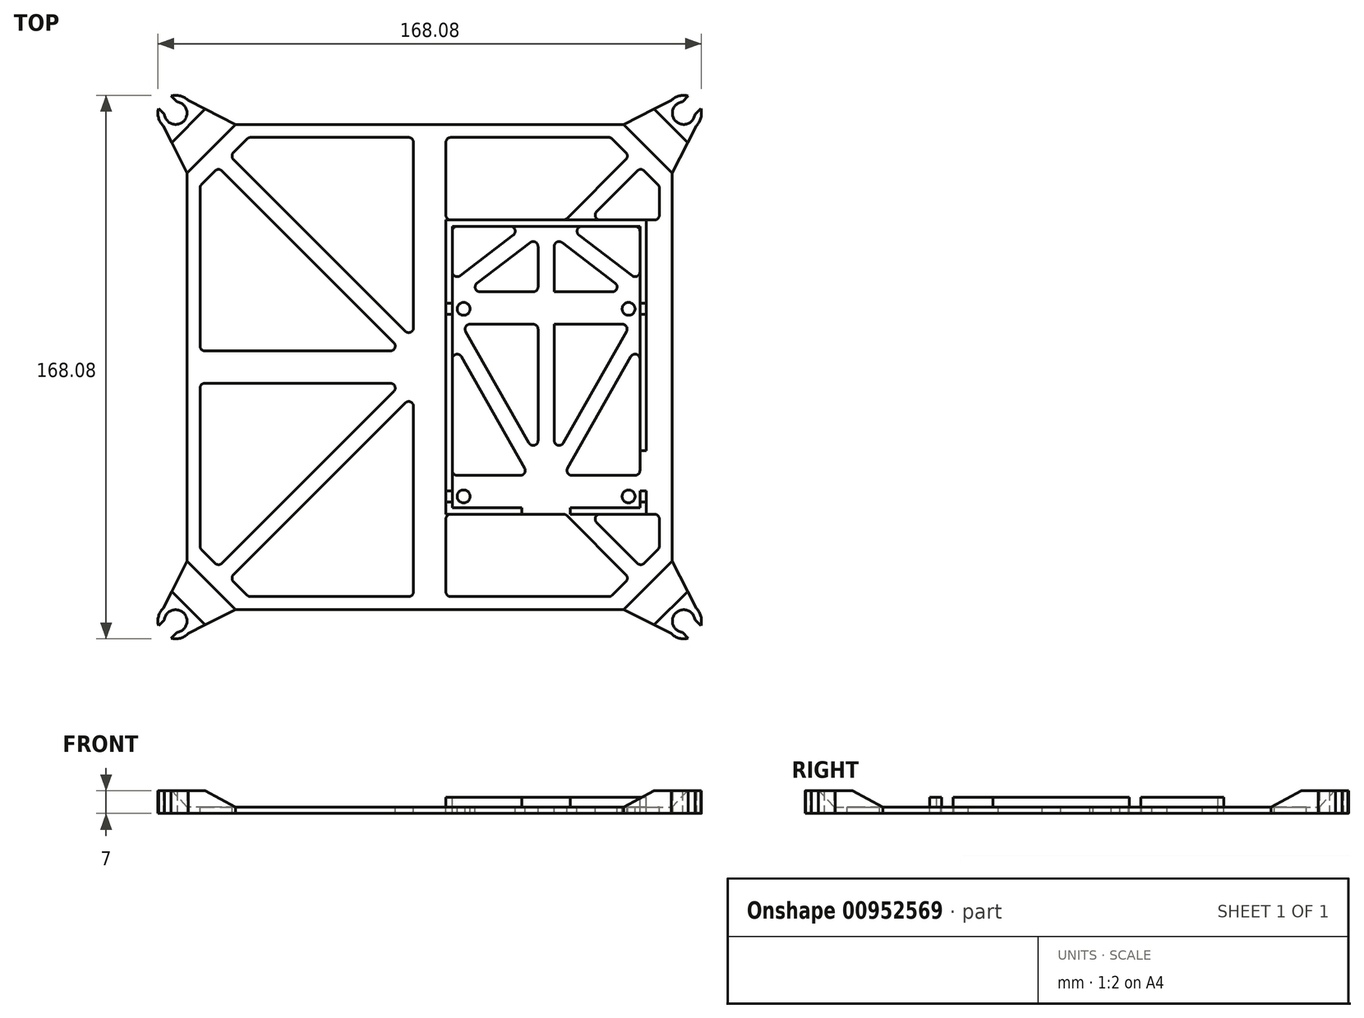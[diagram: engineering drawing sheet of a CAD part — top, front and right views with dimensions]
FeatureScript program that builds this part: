
annotation { "Feature Type Name" : "Feature", "Feature Type Description" : "" }
export const myFeature = defineFeature(function(context is Context, id is Id, definition is map)
    precondition{}
    {
        {
            var Q0;
            Q0=qCreatedBy(makeId("Top.planeOp"),FACE);
            var sketch = newSketch(context, id + "F0", { "sketchPlane" : qUnion([Q0])});
            skLineSegment(sketch, "E0.bottom", {"start": v(-75, 75) * mm, "end": v(75, 75) * mm});
            skLineSegment(sketch, "E0.top", {"start": v(-75, -75) * mm, "end": v(75, -75) * mm});
            skLineSegment(sketch, "E0.left", {"start": v(-75, 75) * mm, "end": v(-75, -75) * mm});
            skLineSegment(sketch, "E0.right", {"start": v(75, 75) * mm, "end": v(75, -75) * mm});
            skPoint(sketch, "E1", {"position": v(0, 75) * mm});
            skPoint(sketch, "E2", {"position": v(-75, 0) * mm});
            skSolve(sketch);
        }
        {
            var Q0;
            Q0=qSketchRegion(id+"F0",true);
            extrude(context, id + "F1", {"entities" : qUnion([Q0]), "depth" : 2 * mm, "offsetDistance" : 25 * mm});
        }
        {
            var Q0;
            Q0=makeQuery(id+"F1.opExtrude","CAP_FACE",FACE,{"disambiguationData":[OSD([sQuery(id+"F0.wireOp",EDGE,"E0.bottom"),sQuery(id+"F0.wireOp",EDGE,"E0.top"),sQuery(id+"F0.wireOp",EDGE,"E0.left"),sQuery(id+"F0.wireOp",EDGE,"E0.right")])],"isStart":false});
            var sketch = newSketch(context, id + "F2", { "sketchPlane" : qUnion([Q0])});
            skLineSegment(sketch, "E3.bottom", {"start": v(7, 43.5) * mm, "end": v(65, 43.5) * mm});
            skLineSegment(sketch, "E3.top", {"start": v(7, -43.5) * mm, "end": v(65, -43.5) * mm});
            skLineSegment(sketch, "E3.left", {"start": v(7, 43.5) * mm, "end": v(7, -43.5) * mm});
            skLineSegment(sketch, "E3.right", {"start": v(65, 43.5) * mm, "end": v(65, -43.5) * mm});
            skPoint(sketch, "E4", {"position": v(36, 43.5) * mm});
            skLineSegment(sketch, "E5.0", {"start": v(5, 45.5) * mm, "end": v(67, 45.5) * mm});
            skLineSegment(sketch, "E5.1", {"start": v(5, 45.5) * mm, "end": v(5, -45.5) * mm});
            skLineSegment(sketch, "E5.2", {"start": v(5, -45.5) * mm, "end": v(67, -45.5) * mm});
            skLineSegment(sketch, "E5.3", {"start": v(67, 45.5) * mm, "end": v(67, -45.5) * mm});
            skPoint(sketch, "E6", {"position": v(7, 0) * mm});
            skSolve(sketch);
        }
        {
            var Q0;
            Q0=qSketchRegion(id+"F2",true);
            extrude(context, id + "F3", {"entities" : qUnion([Q0]), "operationType" : NewBodyOperationType.ADD, "depth" : 3 * mm, "offsetDistance" : 25 * mm});
        }
        {
            var Q0;
            Q0=makeQuery(id+"F3.opExtrude","CAP_FACE",FACE,{"disambiguationData":[OSD([sQuery(id+"F2.wireOp",EDGE,"E3.bottom"),sQuery(id+"F2.wireOp",EDGE,"E3.top"),sQuery(id+"F2.wireOp",EDGE,"E3.left"),sQuery(id+"F2.wireOp",EDGE,"E3.right"),sQuery(id+"F2.wireOp",EDGE,"E5.0"),sQuery(id+"F2.wireOp",EDGE,"E5.1"),sQuery(id+"F2.wireOp",EDGE,"E5.2"),sQuery(id+"F2.wireOp",EDGE,"E5.3")])],"isStart":false});
            var sketch = newSketch(context, id + "F4", { "sketchPlane" : qUnion([Q0])});
            skLineSegment(sketch, "E7.bottom", {"start": v(28.5, -43.5) * mm, "end": v(43.5, -43.5) * mm});
            skLineSegment(sketch, "E7.top", {"start": v(28.5, -45.5) * mm, "end": v(43.5, -45.5) * mm});
            skLineSegment(sketch, "E7.left", {"start": v(28.5, -43.5) * mm, "end": v(28.5, -45.5) * mm});
            skLineSegment(sketch, "E7.right", {"start": v(43.5, -43.5) * mm, "end": v(43.5, -45.5) * mm});
            skLineSegment(sketch, "E8.bottom", {"start": v(67, -39.9) * mm, "end": v(65, -39.9) * mm});
            skLineSegment(sketch, "E8.top", {"start": v(67, -25.9) * mm, "end": v(65, -25.9) * mm});
            skLineSegment(sketch, "E8.left", {"start": v(67, -39.9) * mm, "end": v(67, -25.9) * mm});
            skLineSegment(sketch, "E8.right", {"start": v(65, -39.9) * mm, "end": v(65, -25.9) * mm});
            skPoint(sketch, "E9", {"position": v(36, -43.5) * mm});
            skPoint(sketch, "E10", {"position": v(36, -45.5) * mm});
            skPoint(sketch, "E11", {"position": v(65, -32.9) * mm});
            skSolve(sketch);
        }
        {
            var Q0;
            Q0=qSketchRegion(id+"F4",true);
            extrude(context, id + "F5", {"entities" : qUnion([Q0]), "operationType" : NewBodyOperationType.REMOVE, "oppositeDirection" : true, "depth" : 3 * mm, "offsetDistance" : 25 * mm});
        }
        {
            var Q0;
            {var subQ3=sQuery(id+"F4.wireOp",EDGE,"E7.bottom");Q0=makeQuery(id+"F4.imprint","IMPRINT",FACE,{"disambiguationData":[TD([[makeQuery(id+"F4.imprint","IMPRINT",EDGE,{"derivedFrom":subQ3}),1.0]])]});}
            var sketch = newSketch(context, id + "F6", { "sketchPlane" : qUnion([Q0])});
            skCircle(sketch, "E12", {"center": v(61.5, -40) * mm, "radius": 2 * mm});
            skCircle(sketch, "E13", {"center": v(61.5, 18) * mm, "radius": 2 * mm});
            skLineSegment(sketch, "E14", {"start": v(36, -43.5) * mm, "end": v(36, -14.74) * mm, "construction": true});
            skLineSegment(sketch, "E15.bottom", {"start": v(67, -41.75) * mm, "end": v(65, -41.75) * mm});
            skLineSegment(sketch, "E15.top", {"start": v(67, -38.25) * mm, "end": v(65, -38.25) * mm});
            skLineSegment(sketch, "E15.left", {"start": v(67, -41.75) * mm, "end": v(67, -38.25) * mm});
            skLineSegment(sketch, "E15.right", {"start": v(65, -41.75) * mm, "end": v(65, -38.25) * mm});
            skLineSegment(sketch, "E16.bottom", {"start": v(67, 19.75) * mm, "end": v(65, 19.75) * mm});
            skLineSegment(sketch, "E16.top", {"start": v(67, 16.25) * mm, "end": v(65, 16.25) * mm});
            skLineSegment(sketch, "E16.left", {"start": v(67, 19.75) * mm, "end": v(67, 16.25) * mm});
            skLineSegment(sketch, "E16.right", {"start": v(65, 19.75) * mm, "end": v(65, 16.25) * mm});
            skPoint(sketch, "E17", {"position": v(65, 18) * mm});
            skPoint(sketch, "E18", {"position": v(65, -40) * mm});
            skLineSegment(sketch, "E19.MirrorCS", {"start": v(5, -41.75) * mm, "end": v(7, -41.75) * mm});
            skLineSegment(sketch, "E20.MirrorCS", {"start": v(5, -41.75) * mm, "end": v(5, -38.25) * mm});
            skLineSegment(sketch, "E21.MirrorCS", {"start": v(7, -41.75) * mm, "end": v(7, -38.25) * mm});
            skLineSegment(sketch, "E22.MirrorCS", {"start": v(5, 16.25) * mm, "end": v(7, 16.25) * mm});
            skLineSegment(sketch, "E23.MirrorCS", {"start": v(5, -38.25) * mm, "end": v(7, -38.25) * mm});
            skLineSegment(sketch, "E24.MirrorCS", {"start": v(5, 19.75) * mm, "end": v(5, 16.25) * mm});
            skLineSegment(sketch, "E25.MirrorCS", {"start": v(7, 19.75) * mm, "end": v(7, 16.25) * mm});
            skLineSegment(sketch, "E26.MirrorCS", {"start": v(5, 19.75) * mm, "end": v(7, 19.75) * mm});
            skCircle(sketch, "E27.MirrorC", {"center": v(10.5, 18) * mm, "radius": 2 * mm});
            skCircle(sketch, "E28.MirrorC", {"center": v(10.5, -40) * mm, "radius": 2 * mm});
            skPoint(sketch, "E29.MirrorP", {"position": v(7, 18) * mm});
            skPoint(sketch, "E30.MirrorP", {"position": v(7, -40) * mm});
            skSolve(sketch);
        }
        {
            var Q0;
            Q0 = qSketchRegion(id + "F6", true);
            extrude(context, id + "F7", {"entities" : qUnion([Q0]), "operationType" : NewBodyOperationType.REMOVE, "oppositeDirection" : true, "depth" : 25 * mm, "offsetDistance" : 25 * mm});
        }
        {
            var Q0;
            Q0=makeQuery(id+"F2.imprint","IMPRINT",FACE,{"disambiguationData":[TD([[makeQuery(id+"F2.imprint","IMPRINT",EDGE,{"derivedFrom":sQuery(id+"F2.wireOp",EDGE,"E5.0")}),1.0]])]});
            var sketch = newSketch(context, id + "F8", { "sketchPlane" : qUnion([Q0])});
            skLineSegment(sketch, "E31", {"start": v(75, 75) * mm, "end": v(78.54, 78.54) * mm, "construction": true});
            skLineSegment(sketch, "E32", {"start": v(78.12, 82.01) * mm, "end": v(79.96, 83.85) * mm});
            skLineSegment(sketch, "E33", {"start": v(79.96, 83.85) * mm, "end": v(83.85, 79.96) * mm, "construction": true});
            skLineSegment(sketch, "E34", {"start": v(83.85, 79.96) * mm, "end": v(82.01, 78.12) * mm});
            skLineSegment(sketch, "E35", {"start": v(82.01, 78.12) * mm, "end": v(78.12, 82.01) * mm, "construction": true});
            skPoint(sketch, "E36", {"position": v(80.07, 80.07) * mm});
            skLineSegment(sketch, "E37.MirrorCS", {"start": v(83.85, 79.96) * mm, "end": v(85.69, 81.8) * mm, "construction": true});
            skLineSegment(sketch, "E38.MirrorCS", {"start": v(81.8, 85.69) * mm, "end": v(79.96, 83.85) * mm, "construction": true});
            skLineSegment(sketch, "E39.MirrorCS", {"start": v(85.69, 81.8) * mm, "end": v(81.8, 85.69) * mm, "construction": true});
            skArc(sketch, "E40", {"start": v(79.96, 83.85) * mm, "mid": v(77.11, 83.85) * mm, "end": v(74.65, 82.42) * mm});
            skArc(sketch, "E41", {"start": v(83.85, 79.96) * mm, "mid": v(82.42, 82.42) * mm, "end": v(79.96, 83.85) * mm, "construction": true});
            skArc(sketch, "E42", {"start": v(82.01, 78.12) * mm, "mid": v(81.01, 81.01) * mm, "end": v(78.12, 82.01) * mm, "construction": true});
            skArc(sketch, "E43", {"start": v(78.12, 82.01) * mm, "mid": v(76.06, 76.06) * mm, "end": v(82.01, 78.12) * mm});
            skLineSegment(sketch, "E44", {"start": v(74.65, 82.42) * mm, "end": v(82.42, 74.65) * mm, "construction": true});
            skLineSegment(sketch, "E45", {"start": v(74.65, 82.42) * mm, "end": v(60, 75) * mm});
            skLineSegment(sketch, "E46.MirrorCS", {"start": v(82.42, 74.65) * mm, "end": v(75, 60) * mm});
            skArc(sketch, "E47", {"start": v(82.42, 74.65) * mm, "mid": v(83.85, 77.11) * mm, "end": v(83.85, 79.96) * mm});
            skArc(sketch, "E48", {"start": v(74.65, 82.42) * mm, "mid": v(74.65, 74.65) * mm, "end": v(82.42, 74.65) * mm, "construction": true});
            skLineSegment(sketch, "E49.2.8", {"start": v(-75, -75) * mm, "end": v(75, 75) * mm, "construction": true});
            skLineSegment(sketch, "E50", {"start": v(60, 75) * mm, "end": v(75, 60) * mm});
            skLineSegment(sketch, "E51.1.0", {"start": v(-74.65, 82.42) * mm, "end": v(-60, 75) * mm});
            skArc(sketch, "E51.1.1", {"start": v(-82.42, 74.65) * mm, "mid": v(-74.65, 74.65) * mm, "end": v(-74.65, 82.42) * mm, "construction": true});
            skLineSegment(sketch, "E51.1.2", {"start": v(-82.42, 74.65) * mm, "end": v(-75, 60) * mm});
            skLineSegment(sketch, "E51.1.3", {"start": v(-75, 60) * mm, "end": v(-60, 75) * mm});
            skPoint(sketch, "E51.1.4", {"position": v(-78.54, 78.54) * mm});
            skArc(sketch, "E51.1.5", {"start": v(-82.01, 78.12) * mm, "mid": v(-76.06, 76.06) * mm, "end": v(-78.12, 82.01) * mm});
            skLineSegment(sketch, "E51.1.6", {"start": v(-81.8, 85.69) * mm, "end": v(-85.69, 81.8) * mm, "construction": true});
            skPoint(sketch, "E51.1.7", {"position": v(-80.07, 80.07) * mm});
            skLineSegment(sketch, "E51.1.8", {"start": v(-75, 75) * mm, "end": v(-78.54, 78.54) * mm, "construction": true});
            skLineSegment(sketch, "E51.1.9", {"start": v(-82.42, 74.65) * mm, "end": v(-74.65, 82.42) * mm, "construction": true});
            skArc(sketch, "E51.1.10", {"start": v(-78.12, 82.01) * mm, "mid": v(-81.01, 81.01) * mm, "end": v(-82.01, 78.12) * mm, "construction": true});
            skArc(sketch, "E51.1.11", {"start": v(-74.65, 82.42) * mm, "mid": v(-77.11, 83.85) * mm, "end": v(-79.96, 83.85) * mm});
            skArc(sketch, "E51.1.12", {"start": v(-83.85, 79.96) * mm, "mid": v(-83.85, 77.11) * mm, "end": v(-82.42, 74.65) * mm});
            skLineSegment(sketch, "E51.1.13", {"start": v(-78.12, 82.01) * mm, "end": v(-82.01, 78.12) * mm, "construction": true});
            skLineSegment(sketch, "E51.1.14", {"start": v(-83.85, 79.96) * mm, "end": v(-79.96, 83.85) * mm, "construction": true});
            skLineSegment(sketch, "E51.1.15", {"start": v(-85.69, 81.8) * mm, "end": v(-83.85, 79.96) * mm, "construction": true});
            skLineSegment(sketch, "E51.1.16", {"start": v(-79.96, 83.85) * mm, "end": v(-78.12, 82.01) * mm});
            skLineSegment(sketch, "E51.1.17", {"start": v(-79.96, 83.85) * mm, "end": v(-81.8, 85.69) * mm, "construction": true});
            skArc(sketch, "E51.1.18", {"start": v(-79.96, 83.85) * mm, "mid": v(-82.42, 82.42) * mm, "end": v(-83.85, 79.96) * mm, "construction": true});
            skLineSegment(sketch, "E51.1.19", {"start": v(-82.01, 78.12) * mm, "end": v(-83.85, 79.96) * mm});
            skLineSegment(sketch, "E51.2.0", {"start": v(-82.42, -74.65) * mm, "end": v(-75, -60) * mm});
            skArc(sketch, "E51.2.1", {"start": v(-74.65, -82.42) * mm, "mid": v(-74.65, -74.65) * mm, "end": v(-82.42, -74.65) * mm, "construction": true});
            skLineSegment(sketch, "E51.2.2", {"start": v(-74.65, -82.42) * mm, "end": v(-60, -75) * mm});
            skLineSegment(sketch, "E51.2.3", {"start": v(-60, -75) * mm, "end": v(-75, -60) * mm});
            skPoint(sketch, "E51.2.4", {"position": v(-78.54, -78.54) * mm});
            skArc(sketch, "E51.2.5", {"start": v(-78.12, -82.01) * mm, "mid": v(-76.06, -76.06) * mm, "end": v(-82.01, -78.12) * mm});
            skLineSegment(sketch, "E51.2.6", {"start": v(-85.69, -81.8) * mm, "end": v(-81.8, -85.69) * mm, "construction": true});
            skPoint(sketch, "E51.2.7", {"position": v(-80.07, -80.07) * mm});
            skLineSegment(sketch, "E51.2.8", {"start": v(-75, -75) * mm, "end": v(-78.54, -78.54) * mm, "construction": true});
            skLineSegment(sketch, "E51.2.9", {"start": v(-74.65, -82.42) * mm, "end": v(-82.42, -74.65) * mm, "construction": true});
            skArc(sketch, "E51.2.10", {"start": v(-82.01, -78.12) * mm, "mid": v(-81.01, -81.01) * mm, "end": v(-78.12, -82.01) * mm, "construction": true});
            skArc(sketch, "E51.2.11", {"start": v(-82.42, -74.65) * mm, "mid": v(-83.85, -77.11) * mm, "end": v(-83.85, -79.96) * mm});
            skArc(sketch, "E51.2.12", {"start": v(-79.96, -83.85) * mm, "mid": v(-77.11, -83.85) * mm, "end": v(-74.65, -82.42) * mm});
            skLineSegment(sketch, "E51.2.13", {"start": v(-82.01, -78.12) * mm, "end": v(-78.12, -82.01) * mm, "construction": true});
            skLineSegment(sketch, "E51.2.14", {"start": v(-79.96, -83.85) * mm, "end": v(-83.85, -79.96) * mm, "construction": true});
            skLineSegment(sketch, "E51.2.15", {"start": v(-81.8, -85.69) * mm, "end": v(-79.96, -83.85) * mm, "construction": true});
            skLineSegment(sketch, "E51.2.16", {"start": v(-83.85, -79.96) * mm, "end": v(-82.01, -78.12) * mm});
            skLineSegment(sketch, "E51.2.17", {"start": v(-83.85, -79.96) * mm, "end": v(-85.69, -81.8) * mm, "construction": true});
            skArc(sketch, "E51.2.18", {"start": v(-83.85, -79.96) * mm, "mid": v(-82.42, -82.42) * mm, "end": v(-79.96, -83.85) * mm, "construction": true});
            skLineSegment(sketch, "E51.2.19", {"start": v(-78.12, -82.01) * mm, "end": v(-79.96, -83.85) * mm});
            skPoint(sketch, "E51.center", {"position": v(0, 0) * mm});
            skLineSegment(sketch, "E52.2.3.0", {"start": v(74.65, -82.42) * mm, "end": v(60, -75) * mm});
            skArc(sketch, "E52.3.3.0", {"start": v(82.42, -74.65) * mm, "mid": v(74.65, -74.65) * mm, "end": v(74.65, -82.42) * mm, "construction": true});
            skLineSegment(sketch, "E52.7.3.0", {"start": v(82.42, -74.65) * mm, "end": v(75, -60) * mm});
            skLineSegment(sketch, "E52.10.3.0", {"start": v(75, -60) * mm, "end": v(60, -75) * mm});
            skPoint(sketch, "E52.13.3.0", {"position": v(78.54, -78.54) * mm});
            skArc(sketch, "E52.14.3.0", {"start": v(82.01, -78.12) * mm, "mid": v(76.06, -76.06) * mm, "end": v(78.12, -82.01) * mm});
            skLineSegment(sketch, "E52.18.3.0", {"start": v(81.8, -85.69) * mm, "end": v(85.69, -81.8) * mm, "construction": true});
            skPoint(sketch, "E52.21.3.0", {"position": v(80.07, -80.07) * mm});
            skLineSegment(sketch, "E52.22.3.0", {"start": v(75, -75) * mm, "end": v(78.54, -78.54) * mm, "construction": true});
            skLineSegment(sketch, "E52.25.3.0", {"start": v(82.42, -74.65) * mm, "end": v(74.65, -82.42) * mm, "construction": true});
            skArc(sketch, "E52.28.3.0", {"start": v(78.12, -82.01) * mm, "mid": v(81.01, -81.01) * mm, "end": v(82.01, -78.12) * mm, "construction": true});
            skArc(sketch, "E52.32.3.0", {"start": v(74.65, -82.42) * mm, "mid": v(77.11, -83.85) * mm, "end": v(79.96, -83.85) * mm});
            skArc(sketch, "E52.36.3.0", {"start": v(83.85, -79.96) * mm, "mid": v(83.85, -77.11) * mm, "end": v(82.42, -74.65) * mm});
            skLineSegment(sketch, "E52.40.3.0", {"start": v(78.12, -82.01) * mm, "end": v(82.01, -78.12) * mm, "construction": true});
            skLineSegment(sketch, "E52.43.3.0", {"start": v(83.85, -79.96) * mm, "end": v(79.96, -83.85) * mm, "construction": true});
            skLineSegment(sketch, "E52.46.3.0", {"start": v(85.69, -81.8) * mm, "end": v(83.85, -79.96) * mm, "construction": true});
            skLineSegment(sketch, "E52.49.3.0", {"start": v(79.96, -83.85) * mm, "end": v(78.12, -82.01) * mm});
            skLineSegment(sketch, "E52.52.3.0", {"start": v(79.96, -83.85) * mm, "end": v(81.8, -85.69) * mm, "construction": true});
            skArc(sketch, "E52.55.3.0", {"start": v(79.96, -83.85) * mm, "mid": v(82.42, -82.42) * mm, "end": v(83.85, -79.96) * mm, "construction": true});
            skLineSegment(sketch, "E52.59.3.0", {"start": v(82.01, -78.12) * mm, "end": v(83.85, -79.96) * mm});
            skSolve(sketch);
        }
        {
            var Q0;
            Q0 = qSketchRegion(id + "F8", true);
            extrude(context, id + "F9", {"entities" : qUnion([Q0]), "operationType" : NewBodyOperationType.ADD, "depth" : 5 * mm, "offsetDistance" : 25 * mm, "hasSecondDirection" : true, "secondDirectionOppositeDirection" : true, "secondDirectionDepth" : 2 * mm});
        }
        {
            var Q0;
            Q0 = qSketchRegion(id + "F8", true);
            extrude(context, id + "F10", {"entities" : qUnion([Q0]), "operationType" : NewBodyOperationType.ADD, "depth" : 5 * mm, "offsetDistance" : 25 * mm});
        }
        {
            var Q0;
            Q0 = qSketchRegion(id + "F8", true);
            extrude(context, id + "F11", {"entities" : qUnion([Q0]), "operationType" : NewBodyOperationType.ADD, "depth" : 5 * mm, "offsetDistance" : 25 * mm});
        }
        {
            var Q0;
            Q0=makeQuery(id+"F9.opExtrude","CAP_EDGE",EDGE,{"disambiguationData":[OSD([sQuery(id+"F8.wireOp",EDGE,"E51.1.3")])],"isStart":false});
            var Q1;
            Q1=makeQuery(id+"F9.opExtrude","CAP_EDGE",EDGE,{"disambiguationData":[OSD([sQuery(id+"F8.wireOp",EDGE,"E50")])],"isStart":false});
            var Q2;
            Q2=makeQuery(id+"F9.opExtrude","CAP_EDGE",EDGE,{"disambiguationData":[OSD([sQuery(id+"F8.wireOp",EDGE,"E52.10.3.0")])],"isStart":false});
            var Q3;
            Q3=makeQuery(id+"F9.opExtrude","CAP_EDGE",EDGE,{"disambiguationData":[OSD([sQuery(id+"F8.wireOp",EDGE,"E51.2.3")])],"isStart":false});
            chamfer(context, id + "F12", {"entities" : qUnion([Q0, Q1, Q2, Q3]), "chamferType" : ChamferType.TWO_OFFSETS, "width1" : 10 * mm, "oppositeDirection" : false, "width2" : 5 * mm, "tangentPropagation" : true});
        }
        {
            var Q0;
            Q0=makeQuery(id+"F2.imprint","IMPRINT",FACE,{"disambiguationData":[TD([[makeQuery(id+"F2.imprint","IMPRINT",EDGE,{"derivedFrom":sQuery(id+"F2.wireOp",EDGE,"E5.0")}),1.0]])]});
            var sketch = newSketch(context, id + "F13", { "sketchPlane" : qUnion([Q0])});
            skLineSegment(sketch, "E53", {"start": v(-71, -56) * mm, "end": v(-71, 56) * mm, "construction": true});
            skLineSegment(sketch, "E54", {"start": v(-60.67, 66.33) * mm, "end": v(-56, 71) * mm, "construction": true});
            skLineSegment(sketch, "E55", {"start": v(-75, 60) * mm, "end": v(60, -75) * mm, "construction": true});
            skLineSegment(sketch, "E56", {"start": v(-75, -60) * mm, "end": v(60, 75) * mm, "construction": true});
            skLineSegment(sketch, "E57.1.0", {"start": v(-56, -71) * mm, "end": v(-71, -56) * mm, "construction": true});
            skLineSegment(sketch, "E57.1.1", {"start": v(56, -71) * mm, "end": v(-56, -71) * mm, "construction": true});
            skLineSegment(sketch, "E57.2.0", {"start": v(71, -56) * mm, "end": v(56, -71) * mm, "construction": true});
            skLineSegment(sketch, "E57.2.1", {"start": v(71, 56) * mm, "end": v(71, -56) * mm, "construction": true});
            skLineSegment(sketch, "E57.3.0", {"start": v(56, 71) * mm, "end": v(71, 56) * mm, "construction": true});
            skLineSegment(sketch, "E57.3.1", {"start": v(-56, 71) * mm, "end": v(-6.5, 71) * mm, "construction": true});
            skPoint(sketch, "E57.center", {"position": v(0, 0) * mm});
            skLineSegment(sketch, "E58", {"start": v(-71, 56) * mm, "end": v(-71, -56) * mm});
            skLineSegment(sketch, "E59", {"start": v(-5, 69.5) * mm, "end": v(-5, 12.16) * mm, "construction": true});
            skLineSegment(sketch, "E60", {"start": v(5, 71) * mm, "end": v(5, 45.5) * mm});
            skLineSegment(sketch, "E61", {"start": v(5, -45.5) * mm, "end": v(5, -71) * mm});
            skLineSegment(sketch, "E62", {"start": v(-71, 5) * mm, "end": v(-8.54, 5) * mm});
            skLineSegment(sketch, "E63", {"start": v(-71, -5) * mm, "end": v(0, -5) * mm});
            skLineSegment(sketch, "E64", {"start": v(-60.67, 64.2) * mm, "end": v(-7.56, 11.1) * mm});
            skLineSegment(sketch, "E65", {"start": v(-65.27, 61.73) * mm, "end": v(-8.54, 5) * mm});
            skPoint(sketch, "E66", {"position": v(-63.5, 63.5) * mm});
            skLineSegment(sketch, "E67", {"start": v(-63.5, 63.5) * mm, "end": v(75.2, -75.2) * mm, "construction": true});
            skLineSegment(sketch, "E68", {"start": v(-5, 71) * mm, "end": v(-56, 71) * mm});
            skLineSegment(sketch, "E69", {"start": v(-61.73, 65.27) * mm, "end": v(-56, 71) * mm});
            skLineSegment(sketch, "E70", {"start": v(-65.27, 61.73) * mm, "end": v(-71, 56) * mm});
            skLineSegment(sketch, "E71", {"start": v(-71, 5) * mm, "end": v(-71, 56) * mm});
            skLineSegment(sketch, "E72", {"start": v(0, 0) * mm, "end": v(-75, 0) * mm, "construction": true});
            skLineSegment(sketch, "E73.MirrorCS", {"start": v(-71, -5) * mm, "end": v(-71, -56) * mm});
            skLineSegment(sketch, "E74.MirrorCS", {"start": v(-65.27, -61.73) * mm, "end": v(-71, -56) * mm});
            skLineSegment(sketch, "E75.MirrorCS", {"start": v(-61.73, -65.27) * mm, "end": v(-56, -71) * mm});
            skLineSegment(sketch, "E76.MirrorCS", {"start": v(-5, -71) * mm, "end": v(-56, -71) * mm});
            skLineSegment(sketch, "E77.MirrorCS", {"start": v(-71, -56) * mm, "end": v(-71, 56) * mm});
            skLineSegment(sketch, "E78.MirrorCS", {"start": v(-61.73, -65.27) * mm, "end": v(-5, -8.54) * mm});
            skLineSegment(sketch, "E79.MirrorCS", {"start": v(-65.27, -61.73) * mm, "end": v(-8.54, -5) * mm});
            skPoint(sketch, "E80.MirrorP", {"position": v(-63.5, -63.5) * mm});
            skLineSegment(sketch, "E81.MirrorCS", {"start": v(-56, -71) * mm, "end": v(56, -71) * mm, "construction": true});
            skLineSegment(sketch, "E82.MirrorCS", {"start": v(-71, -56) * mm, "end": v(-56, -71) * mm, "construction": true});
            skLineSegment(sketch, "E83.MirrorCS", {"start": v(-63.5, -63.5) * mm, "end": v(75.2, 75.2) * mm, "construction": true});
            skLineSegment(sketch, "E84.MirrorCS", {"start": v(-5, -71) * mm, "end": v(-5, 8.54) * mm});
            skLineSegment(sketch, "E85", {"start": v(-5, 8.54) * mm, "end": v(-5, 71) * mm});
            skLineSegment(sketch, "E86", {"start": v(-8.54, 5) * mm, "end": v(0, 5) * mm, "construction": true});
            skLineSegment(sketch, "E87", {"start": v(-5, 8.54) * mm, "end": v(-5, 71) * mm, "construction": true});
            skLineSegment(sketch, "E88", {"start": v(-5, -8.54) * mm, "end": v(-5, -71) * mm, "construction": true});
            skLineSegment(sketch, "E89", {"start": v(5, -71) * mm, "end": v(56, -71) * mm});
            skLineSegment(sketch, "E90", {"start": v(5, 71) * mm, "end": v(56, 71) * mm});
            skLineSegment(sketch, "E91", {"start": v(56, 71) * mm, "end": v(61.73, 65.27) * mm});
            skLineSegment(sketch, "E92", {"start": v(61.73, 65.27) * mm, "end": v(41.96, 45.5) * mm});
            skLineSegment(sketch, "E93", {"start": v(41.96, 45.5) * mm, "end": v(5, 45.5) * mm});
            skLineSegment(sketch, "E94", {"start": v(5, -45.5) * mm, "end": v(41.96, -45.5) * mm});
            skLineSegment(sketch, "E95", {"start": v(41.96, -45.5) * mm, "end": v(61.73, -65.27) * mm});
            skLineSegment(sketch, "E96", {"start": v(61.73, -65.27) * mm, "end": v(56, -71) * mm});
            skLineSegment(sketch, "E97", {"start": v(65.27, 61.73) * mm, "end": v(49.04, 45.5) * mm});
            skLineSegment(sketch, "E98", {"start": v(49.04, 45.5) * mm, "end": v(71, 45.5) * mm});
            skLineSegment(sketch, "E99", {"start": v(71, 45.5) * mm, "end": v(71, 56) * mm});
            skLineSegment(sketch, "E100", {"start": v(65.27, 61.73) * mm, "end": v(71, 56) * mm});
            skLineSegment(sketch, "E101", {"start": v(49.04, -45.5) * mm, "end": v(65.27, -61.73) * mm});
            skLineSegment(sketch, "E102", {"start": v(65.27, -61.73) * mm, "end": v(71, -56) * mm});
            skLineSegment(sketch, "E103", {"start": v(71, -45.5) * mm, "end": v(49.04, -45.5) * mm});
            skLineSegment(sketch, "E104", {"start": v(71, -45.5) * mm, "end": v(71, -56) * mm});
            skPoint(sketch, "E105.newPointA", {"position": v(56, 71) * mm});
            skPoint(sketch, "E105.newPointB", {"position": v(-5, 71) * mm});
            skArc(sketch, "E105.filletArc", {"start": v(-5, 69.5) * mm, "mid": v(-5.44, 70.56) * mm, "end": v(-6.5, 71) * mm, "construction": true});
            skPoint(sketch, "E106.newPointA", {"position": v(-71, 56) * mm});
            skPoint(sketch, "E106.newPointB", {"position": v(-61.73, 65.27) * mm});
            skArc(sketch, "E106.filletArc", {"start": v(-60.67, 66.33) * mm, "mid": v(-61.11, 65.27) * mm, "end": v(-60.67, 64.2) * mm});
            skPoint(sketch, "E107.newPointA", {"position": v(-5, -71) * mm});
            skPoint(sketch, "E107.newPointB", {"position": v(-5, 8.54) * mm});
            skArc(sketch, "E107.filletArc", {"start": v(-7.56, 11.1) * mm, "mid": v(-5.93, 10.77) * mm, "end": v(-5, 12.16) * mm});
            skSolve(sketch);
        }
        {
            var Q0;
            Q0 = qSketchRegion(id + "F13", true);
            extrude(context, id + "F14", {"entities" : qUnion([Q0]), "operationType" : NewBodyOperationType.REMOVE, "oppositeDirection" : true, "depth" : 25 * mm, "offsetDistance" : 25 * mm});
        }
        {
            var Q0;
            {var subQ3=sQuery(id+"F4.wireOp",EDGE,"E7.bottom");Q0=makeQuery(id+"F4.imprint","IMPRINT",FACE,{"disambiguationData":[TD([[makeQuery(id+"F4.imprint","IMPRINT",EDGE,{"derivedFrom":subQ3}),1.0]])]});}
            var sketch = newSketch(context, id + "F15", { "sketchPlane" : qUnion([Q0])});
            skLineSegment(sketch, "E108", {"start": v(7, 23.25) * mm, "end": v(11.12, 23.25) * mm, "construction": true});
            skLineSegment(sketch, "E109", {"start": v(7, 13.25) * mm, "end": v(9.87, 13.25) * mm, "construction": true});
            skLineSegment(sketch, "E110", {"start": v(33.5, 43.5) * mm, "end": v(33.5, 40.35) * mm, "construction": true});
            skLineSegment(sketch, "E111", {"start": v(38.5, 43.5) * mm, "end": v(38.5, 23.25) * mm});
            skLineSegment(sketch, "E112", {"start": v(8.5, -33.5) * mm, "end": v(28.05, -33.5) * mm});
            skLineSegment(sketch, "E113", {"start": v(33.5, 11.75) * mm, "end": v(33.5, -22.74) * mm});
            skLineSegment(sketch, "E114", {"start": v(38.5, 13.25) * mm, "end": v(38.5, -33.5) * mm});
            skLineSegment(sketch, "E115", {"start": v(7, 23.25) * mm, "end": v(7, 13.25) * mm, "construction": true});
            skPoint(sketch, "E116", {"position": v(7, 18.25) * mm});
            skLineSegment(sketch, "E117", {"start": v(33.5, 43.5) * mm, "end": v(38.5, 43.5) * mm, "construction": true});
            skPoint(sketch, "E118", {"position": v(36, 43.5) * mm});
            skLineSegment(sketch, "E119", {"start": v(38.5, 23.25) * mm, "end": v(65, 23.25) * mm});
            skLineSegment(sketch, "E120", {"start": v(33.5, 23.25) * mm, "end": v(38.5, 23.25) * mm, "construction": true});
            skLineSegment(sketch, "E121", {"start": v(33.5, 13.25) * mm, "end": v(38.5, 13.25) * mm, "construction": true});
            skLineSegment(sketch, "E122", {"start": v(38.5, 13.25) * mm, "end": v(65, 13.25) * mm});
            skLineSegment(sketch, "E123", {"start": v(38.5, -33.5) * mm, "end": v(38.5, -33.5) * mm});
            skLineSegment(sketch, "E124", {"start": v(33.5, -33.5) * mm, "end": v(38.5, -33.5) * mm, "construction": true});
            skLineSegment(sketch, "E125", {"start": v(38.5, -33.5) * mm, "end": v(65, -33.5) * mm});
            skLineSegment(sketch, "E126", {"start": v(11.14, 11.01) * mm, "end": v(30.7, -23.48) * mm});
            skLineSegment(sketch, "E127", {"start": v(9.8, 3.23) * mm, "end": v(29.36, -31.26) * mm});
            skLineSegment(sketch, "E128", {"start": v(7, 13.25) * mm, "end": v(33.5, -33.5) * mm, "construction": true});
            skLineSegment(sketch, "E129", {"start": v(12.45, 13.25) * mm, "end": v(32, 13.25) * mm});
            skLineSegment(sketch, "E130", {"start": v(7, 2.5) * mm, "end": v(7, -32) * mm});
            skPoint(sketch, "E131.visualSharp", {"position": v(7, 8.18) * mm});
            skArc(sketch, "E131.filletArc", {"start": v(9.8, 3.23) * mm, "mid": v(8.12, 3.94) * mm, "end": v(7, 2.5) * mm});
            skArc(sketch, "E132.filletArc", {"start": v(28.05, -33.5) * mm, "mid": v(29.35, -32.76) * mm, "end": v(29.36, -31.26) * mm});
            skPoint(sketch, "E133.visualSharp", {"position": v(7, -33.5) * mm});
            skArc(sketch, "E133.filletArc", {"start": v(7, -32) * mm, "mid": v(7.44, -33.06) * mm, "end": v(8.5, -33.5) * mm});
            skPoint(sketch, "E134.visualSharp", {"position": v(9.87, 13.25) * mm});
            skArc(sketch, "E134.filletArc", {"start": v(12.45, 13.25) * mm, "mid": v(11.15, 12.5) * mm, "end": v(11.14, 11.01) * mm});
            skPoint(sketch, "E135.visualSharp", {"position": v(33.5, 13.25) * mm});
            skArc(sketch, "E135.filletArc", {"start": v(33.5, 11.75) * mm, "mid": v(33.06, 12.81) * mm, "end": v(32, 13.25) * mm});
            skArc(sketch, "E136.filletArc", {"start": v(30.7, -23.48) * mm, "mid": v(32.38, -24.2) * mm, "end": v(33.5, -22.74) * mm});
            skLineSegment(sketch, "E137", {"start": v(36, -43.5) * mm, "end": v(36, -5.37) * mm, "construction": true});
            skArc(sketch, "E138.MirrorCS", {"start": v(65, -32) * mm, "mid": v(64.56, -33.06) * mm, "end": v(63.5, -33.5) * mm});
            skArc(sketch, "E139.MirrorCS", {"start": v(62.2, 3.23) * mm, "mid": v(63.88, 3.94) * mm, "end": v(65, 2.5) * mm});
            skArc(sketch, "E140.MirrorCS", {"start": v(43.95, -33.5) * mm, "mid": v(42.65, -32.76) * mm, "end": v(42.64, -31.26) * mm});
            skArc(sketch, "E141.MirrorCS", {"start": v(38.5, 11.75) * mm, "mid": v(38.94, 12.81) * mm, "end": v(40, 13.25) * mm});
            skLineSegment(sketch, "E142.MirrorCS", {"start": v(38.5, 13.25) * mm, "end": v(33.5, 13.25) * mm, "construction": true});
            skLineSegment(sketch, "E143.MirrorCS", {"start": v(65, 13.25) * mm, "end": v(62.13, 13.25) * mm, "construction": true});
            skArc(sketch, "E144.MirrorCS", {"start": v(59.55, 13.25) * mm, "mid": v(60.85, 12.5) * mm, "end": v(60.86, 11.01) * mm});
            skLineSegment(sketch, "E145.MirrorCS", {"start": v(38.5, -33.5) * mm, "end": v(33.5, -33.5) * mm, "construction": true});
            skArc(sketch, "E146.MirrorCS", {"start": v(41.3, -23.48) * mm, "mid": v(39.62, -24.2) * mm, "end": v(38.5, -22.74) * mm});
            skLineSegment(sketch, "E147.MirrorCS", {"start": v(65, 13.25) * mm, "end": v(38.5, -33.5) * mm, "construction": true});
            skLineSegment(sketch, "E148.MirrorCS", {"start": v(65, 23.25) * mm, "end": v(65, 13.25) * mm, "construction": true});
            skLineSegment(sketch, "E149.MirrorCS", {"start": v(60.86, 11.01) * mm, "end": v(41.3, -23.48) * mm});
            skPoint(sketch, "E150.MirrorP", {"position": v(65, 18.25) * mm});
            skLineSegment(sketch, "E151.MirrorCS", {"start": v(62.2, 3.23) * mm, "end": v(42.64, -31.26) * mm});
            skPoint(sketch, "E152.MirrorP", {"position": v(38.5, 13.25) * mm});
            skPoint(sketch, "E153.MirrorP", {"position": v(65, 8.18) * mm});
            skLineSegment(sketch, "E154.MirrorCS", {"start": v(63.5, -33.5) * mm, "end": v(43.95, -33.5) * mm});
            skLineSegment(sketch, "E155.MirrorCS", {"start": v(59.55, 13.25) * mm, "end": v(40, 13.25) * mm});
            skPoint(sketch, "E156.MirrorP", {"position": v(65, -33.5) * mm});
            skLineSegment(sketch, "E157.MirrorCS", {"start": v(38.5, 11.75) * mm, "end": v(38.5, -22.74) * mm});
            skPoint(sketch, "E158.MirrorP", {"position": v(62.13, 13.25) * mm});
            skLineSegment(sketch, "E159.MirrorCS", {"start": v(65, 2.5) * mm, "end": v(65, -32) * mm});
            skLineSegment(sketch, "E160", {"start": v(31.09, 38.51) * mm, "end": v(14.64, 25.94) * mm});
            skLineSegment(sketch, "E161", {"start": v(33.5, 43.5) * mm, "end": v(7, 23.25) * mm, "construction": true});
            skLineSegment(sketch, "E162", {"start": v(33.5, 37.32) * mm, "end": v(33.5, 24.75) * mm});
            skLineSegment(sketch, "E163", {"start": v(15.55, 23.25) * mm, "end": v(32, 23.25) * mm});
            skPoint(sketch, "E164.visualSharp", {"position": v(33.5, 40.35) * mm});
            skArc(sketch, "E164.filletArc", {"start": v(33.5, 37.32) * mm, "mid": v(32.66, 38.66) * mm, "end": v(31.09, 38.51) * mm});
            skPoint(sketch, "E165.visualSharp", {"position": v(33.5, 23.25) * mm});
            skArc(sketch, "E165.filletArc", {"start": v(32, 23.25) * mm, "mid": v(33.06, 23.69) * mm, "end": v(33.5, 24.75) * mm});
            skPoint(sketch, "E166.visualSharp", {"position": v(11.12, 23.25) * mm});
            skArc(sketch, "E166.filletArc", {"start": v(14.64, 25.94) * mm, "mid": v(14.13, 24.27) * mm, "end": v(15.55, 23.25) * mm});
            skPoint(sketch, "E167", {"position": v(20.25, 33.38) * mm});
            skLineSegment(sketch, "E168.1.0", {"start": v(7, 29.43) * mm, "end": v(7, 42) * mm});
            skArc(sketch, "E168.1.1", {"start": v(7, 29.43) * mm, "mid": v(7.84, 28.09) * mm, "end": v(9.41, 28.24) * mm});
            skLineSegment(sketch, "E168.1.2", {"start": v(9.41, 28.24) * mm, "end": v(25.86, 40.8) * mm});
            skArc(sketch, "E168.1.3", {"start": v(25.86, 40.8) * mm, "mid": v(26.37, 42.48) * mm, "end": v(24.95, 43.5) * mm});
            skLineSegment(sketch, "E168.1.4", {"start": v(24.95, 43.5) * mm, "end": v(8.5, 43.5) * mm});
            skArc(sketch, "E168.1.5", {"start": v(8.5, 43.5) * mm, "mid": v(7.44, 43.06) * mm, "end": v(7, 42) * mm});
            skLineSegment(sketch, "E169", {"start": v(36, 43.5) * mm, "end": v(36, 23.25) * mm, "construction": true});
            skArc(sketch, "E170.MirrorCS", {"start": v(40, 23.25) * mm, "mid": v(38.94, 23.69) * mm, "end": v(38.5, 24.75) * mm});
            skArc(sketch, "E171.MirrorCS", {"start": v(46.14, 40.8) * mm, "mid": v(45.63, 42.48) * mm, "end": v(47.05, 43.5) * mm});
            skArc(sketch, "E172.MirrorCS", {"start": v(63.5, 43.5) * mm, "mid": v(64.56, 43.06) * mm, "end": v(65, 42) * mm});
            skLineSegment(sketch, "E173.MirrorCS", {"start": v(38.5, 43.5) * mm, "end": v(38.5, 40.35) * mm, "construction": true});
            skArc(sketch, "E174.MirrorCS", {"start": v(38.5, 37.32) * mm, "mid": v(39.34, 38.66) * mm, "end": v(40.91, 38.51) * mm});
            skArc(sketch, "E175.MirrorCS", {"start": v(65, 29.43) * mm, "mid": v(64.16, 28.09) * mm, "end": v(62.59, 28.24) * mm});
            skArc(sketch, "E176.MirrorCS", {"start": v(57.36, 25.94) * mm, "mid": v(57.87, 24.27) * mm, "end": v(56.45, 23.25) * mm});
            skPoint(sketch, "E177.MirrorP", {"position": v(51.75, 33.37) * mm});
            skPoint(sketch, "E178.MirrorP", {"position": v(38.5, 23.25) * mm});
            skLineSegment(sketch, "E179.MirrorCS", {"start": v(38.5, 43.5) * mm, "end": v(65, 23.25) * mm, "construction": true});
            skLineSegment(sketch, "E180.MirrorCS", {"start": v(65, 23.25) * mm, "end": v(60.88, 23.25) * mm, "construction": true});
            skLineSegment(sketch, "E181.MirrorCS", {"start": v(40.91, 38.51) * mm, "end": v(57.36, 25.94) * mm});
            skPoint(sketch, "E182.MirrorP", {"position": v(38.5, 40.35) * mm});
            skLineSegment(sketch, "E183.MirrorCS", {"start": v(62.59, 28.24) * mm, "end": v(46.14, 40.8) * mm});
            skPoint(sketch, "E184.MirrorP", {"position": v(60.88, 23.25) * mm});
            skLineSegment(sketch, "E185.MirrorCS", {"start": v(65, 29.43) * mm, "end": v(65, 42) * mm});
            skLineSegment(sketch, "E186.MirrorCS", {"start": v(38.5, 37.32) * mm, "end": v(38.5, 24.75) * mm});
            skLineSegment(sketch, "E187.MirrorCS", {"start": v(47.05, 43.5) * mm, "end": v(63.5, 43.5) * mm});
            skLineSegment(sketch, "E188.MirrorCS", {"start": v(56.45, 23.25) * mm, "end": v(40, 23.25) * mm});
            skSolve(sketch);
        }
        {
            var Q0;
            Q0 = qSketchRegion(id + "F15", true);
            extrude(context, id + "F16", {"entities" : qUnion([Q0]), "operationType" : NewBodyOperationType.REMOVE, "oppositeDirection" : true, "depth" : 25 * mm, "offsetDistance" : 25 * mm});
        }
        {
            var Q0;
            Q0=makeQuery(id+"F14.boolean.opBoolean","COPY",EDGE,{"derivedFrom":makeQuery(id+"F14.opExtrude","SWEPT_EDGE",EDGE,{"disambiguationData":[OSD([sQuery(id+"F13.wireOp",EDGE,"E68"),sQuery(id+"F13.wireOp",EDGE,"E69")])]})});
            fillet(context, id + "F17", {"entities" : qUnion([Q0]), "radius" : 1.5 * mm, "tangentPropagation" : true, "allowEdgeOverflow" : false});
        }
        {
            var Q0;
            Q0=makeQuery(id+"F14.boolean.opBoolean","COPY",EDGE,{"derivedFrom":makeQuery(id+"F14.opExtrude","SWEPT_EDGE",EDGE,{"disambiguationData":[OSD([sQuery(id+"F13.wireOp",EDGE,"E68"),sQuery(id+"F13.wireOp",EDGE,"E85")])]})});
            var Q1;
            Q1=makeQuery(id+"F14.boolean.opBoolean","COPY",EDGE,{"derivedFrom":makeQuery(id+"F14.opExtrude","SWEPT_EDGE",EDGE,{"disambiguationData":[OSD([sQuery(id+"F13.wireOp",EDGE,"E62"),sQuery(id+"F13.wireOp",EDGE,"E65")])]})});
            var Q2;
            Q2=makeQuery(id+"F14.boolean.opBoolean","COPY",EDGE,{"derivedFrom":makeQuery(id+"F14.opExtrude","SWEPT_EDGE",EDGE,{"disambiguationData":[OSD([sQuery(id+"F13.wireOp",EDGE,"E62"),sQuery(id+"F13.wireOp",EDGE,"E77.MirrorCS")])]})});
            var Q3;
            Q3=makeQuery(id+"F14.boolean.opBoolean","COPY",EDGE,{"derivedFrom":makeQuery(id+"F14.opExtrude","SWEPT_EDGE",EDGE,{"disambiguationData":[OSD([sQuery(id+"F13.wireOp",EDGE,"E65"),sQuery(id+"F13.wireOp",EDGE,"E70")])]})});
            var Q4;
            Q4=makeQuery(id+"F14.boolean.opBoolean","COPY",EDGE,{"derivedFrom":makeQuery(id+"F14.opExtrude","SWEPT_EDGE",EDGE,{"disambiguationData":[OSD([sQuery(id+"F13.wireOp",EDGE,"E70"),sQuery(id+"F13.wireOp",EDGE,"E77.MirrorCS")])]})});
            fillet(context, id + "F18", {"entities" : qUnion([Q0, Q1, Q2, Q3, Q4]), "radius" : 1.5 * mm, "tangentPropagation" : true, "allowEdgeOverflow" : false});
        }
        {
            var Q0;
            Q0=makeQuery(id+"F14.boolean.opBoolean","COPY",EDGE,{"derivedFrom":makeQuery(id+"F14.opExtrude","SWEPT_EDGE",EDGE,{"disambiguationData":[OSD([sQuery(id+"F13.wireOp",EDGE,"E78.MirrorCS"),sQuery(id+"F13.wireOp",EDGE,"E84.MirrorCS")])]})});
            var Q1;
            Q1=makeQuery(id+"F14.boolean.opBoolean","COPY",EDGE,{"derivedFrom":makeQuery(id+"F14.opExtrude","SWEPT_EDGE",EDGE,{"disambiguationData":[OSD([sQuery(id+"F13.wireOp",EDGE,"E63"),sQuery(id+"F13.wireOp",EDGE,"E79.MirrorCS")])]})});
            var Q2;
            Q2=makeQuery(id+"F14.boolean.opBoolean","COPY",EDGE,{"derivedFrom":makeQuery(id+"F14.opExtrude","SWEPT_EDGE",EDGE,{"disambiguationData":[OSD([sQuery(id+"F13.wireOp",EDGE,"E77.MirrorCS"),sQuery(id+"F13.wireOp",EDGE,"E63")])]})});
            var Q3;
            Q3=makeQuery(id+"F14.boolean.opBoolean","COPY",EDGE,{"derivedFrom":makeQuery(id+"F14.opExtrude","SWEPT_EDGE",EDGE,{"disambiguationData":[OSD([sQuery(id+"F13.wireOp",EDGE,"E74.MirrorCS"),sQuery(id+"F13.wireOp",EDGE,"E77.MirrorCS")])]})});
            var Q4;
            Q4=makeQuery(id+"F14.boolean.opBoolean","COPY",EDGE,{"derivedFrom":makeQuery(id+"F14.opExtrude","SWEPT_EDGE",EDGE,{"disambiguationData":[OSD([sQuery(id+"F13.wireOp",EDGE,"E75.MirrorCS"),sQuery(id+"F13.wireOp",EDGE,"E78.MirrorCS")])]})});
            var Q5;
            Q5=makeQuery(id+"F14.boolean.opBoolean","COPY",EDGE,{"derivedFrom":makeQuery(id+"F14.opExtrude","SWEPT_EDGE",EDGE,{"disambiguationData":[OSD([sQuery(id+"F13.wireOp",EDGE,"E74.MirrorCS"),sQuery(id+"F13.wireOp",EDGE,"E79.MirrorCS")])]})});
            var Q6;
            Q6=makeQuery(id+"F14.boolean.opBoolean","COPY",EDGE,{"derivedFrom":makeQuery(id+"F14.opExtrude","SWEPT_EDGE",EDGE,{"disambiguationData":[OSD([sQuery(id+"F13.wireOp",EDGE,"E75.MirrorCS"),sQuery(id+"F13.wireOp",EDGE,"E76.MirrorCS")])]})});
            var Q7;
            Q7=makeQuery(id+"F14.boolean.opBoolean","COPY",EDGE,{"derivedFrom":makeQuery(id+"F14.opExtrude","SWEPT_EDGE",EDGE,{"disambiguationData":[OSD([sQuery(id+"F13.wireOp",EDGE,"E76.MirrorCS"),sQuery(id+"F13.wireOp",EDGE,"E84.MirrorCS")])]})});
            var Q8;
            Q8=makeQuery(id+"F14.boolean.opBoolean","COPY",EDGE,{"derivedFrom":makeQuery(id+"F14.opExtrude","SWEPT_EDGE",EDGE,{"disambiguationData":[OSD([sQuery(id+"F13.wireOp",EDGE,"E61"),sQuery(id+"F13.wireOp",EDGE,"E89")])]})});
            var Q9;
            Q9=makeQuery(id+"F14.boolean.opBoolean","COPY",EDGE,{"derivedFrom":makeQuery(id+"F14.opExtrude","SWEPT_EDGE",EDGE,{"disambiguationData":[OSD([sQuery(id+"F2.wireOp",EDGE,"E5.1"),sQuery(id+"F13.wireOp",EDGE,"E61"),sQuery(id+"F13.wireOp",EDGE,"E94")])]})});
            var Q10;
            Q10=makeQuery(id+"F14.boolean.opBoolean","COPY",EDGE,{"derivedFrom":makeQuery(id+"F14.opExtrude","SWEPT_EDGE",EDGE,{"disambiguationData":[OSD([sQuery(id+"F2.wireOp",EDGE,"E5.2"),sQuery(id+"F13.wireOp",EDGE,"E101"),sQuery(id+"F13.wireOp",EDGE,"E103")])]})});
            var Q11;
            Q11=makeQuery(id+"F14.boolean.opBoolean","COPY",EDGE,{"derivedFrom":makeQuery(id+"F14.opExtrude","SWEPT_EDGE",EDGE,{"disambiguationData":[OSD([sQuery(id+"F2.wireOp",EDGE,"E5.2"),sQuery(id+"F13.wireOp",EDGE,"E94"),sQuery(id+"F13.wireOp",EDGE,"E95")])]})});
            var Q12;
            Q12=makeQuery(id+"F14.boolean.opBoolean","COPY",EDGE,{"derivedFrom":makeQuery(id+"F14.opExtrude","SWEPT_EDGE",EDGE,{"disambiguationData":[OSD([sQuery(id+"F13.wireOp",EDGE,"E103"),sQuery(id+"F13.wireOp",EDGE,"E104")])]})});
            var Q13;
            Q13=makeQuery(id+"F14.boolean.opBoolean","COPY",EDGE,{"derivedFrom":makeQuery(id+"F14.opExtrude","SWEPT_EDGE",EDGE,{"disambiguationData":[OSD([sQuery(id+"F13.wireOp",EDGE,"E102"),sQuery(id+"F13.wireOp",EDGE,"E104")])]})});
            var Q14;
            Q14=makeQuery(id+"F14.boolean.opBoolean","COPY",EDGE,{"derivedFrom":makeQuery(id+"F14.opExtrude","SWEPT_EDGE",EDGE,{"disambiguationData":[OSD([sQuery(id+"F13.wireOp",EDGE,"E101"),sQuery(id+"F13.wireOp",EDGE,"E102")])]})});
            var Q15;
            Q15=makeQuery(id+"F14.boolean.opBoolean","COPY",EDGE,{"derivedFrom":makeQuery(id+"F14.opExtrude","SWEPT_EDGE",EDGE,{"disambiguationData":[OSD([sQuery(id+"F13.wireOp",EDGE,"E97"),sQuery(id+"F13.wireOp",EDGE,"E100")])]})});
            var Q16;
            Q16=makeQuery(id+"F14.boolean.opBoolean","COPY",EDGE,{"derivedFrom":makeQuery(id+"F14.opExtrude","SWEPT_EDGE",EDGE,{"disambiguationData":[OSD([sQuery(id+"F13.wireOp",EDGE,"E90"),sQuery(id+"F13.wireOp",EDGE,"E91")])]})});
            var Q17;
            Q17=makeQuery(id+"F14.boolean.opBoolean","COPY",EDGE,{"derivedFrom":makeQuery(id+"F14.opExtrude","SWEPT_EDGE",EDGE,{"disambiguationData":[OSD([sQuery(id+"F13.wireOp",EDGE,"E91"),sQuery(id+"F13.wireOp",EDGE,"E92")])]})});
            var Q18;
            Q18=makeQuery(id+"F14.boolean.opBoolean","COPY",EDGE,{"derivedFrom":makeQuery(id+"F14.opExtrude","SWEPT_EDGE",EDGE,{"disambiguationData":[OSD([sQuery(id+"F13.wireOp",EDGE,"E99"),sQuery(id+"F13.wireOp",EDGE,"E100")])]})});
            var Q19;
            Q19=makeQuery(id+"F14.boolean.opBoolean","COPY",EDGE,{"derivedFrom":makeQuery(id+"F14.opExtrude","SWEPT_EDGE",EDGE,{"disambiguationData":[OSD([sQuery(id+"F13.wireOp",EDGE,"E98"),sQuery(id+"F13.wireOp",EDGE,"E99")])]})});
            var Q20;
            Q20=makeQuery(id+"F14.boolean.opBoolean","COPY",EDGE,{"derivedFrom":makeQuery(id+"F14.opExtrude","SWEPT_EDGE",EDGE,{"disambiguationData":[OSD([sQuery(id+"F2.wireOp",EDGE,"E5.0"),sQuery(id+"F13.wireOp",EDGE,"E97"),sQuery(id+"F13.wireOp",EDGE,"E98")])]})});
            var Q21;
            Q21=makeQuery(id+"F14.boolean.opBoolean","COPY",EDGE,{"derivedFrom":makeQuery(id+"F14.opExtrude","SWEPT_EDGE",EDGE,{"disambiguationData":[OSD([sQuery(id+"F2.wireOp",EDGE,"E5.0"),sQuery(id+"F13.wireOp",EDGE,"E92"),sQuery(id+"F13.wireOp",EDGE,"E93")])]})});
            var Q22;
            Q22=makeQuery(id+"F14.boolean.opBoolean","COPY",EDGE,{"derivedFrom":makeQuery(id+"F14.opExtrude","SWEPT_EDGE",EDGE,{"disambiguationData":[OSD([sQuery(id+"F2.wireOp",EDGE,"E5.1"),sQuery(id+"F13.wireOp",EDGE,"E60"),sQuery(id+"F13.wireOp",EDGE,"E93")])]})});
            var Q23;
            Q23=makeQuery(id+"F14.boolean.opBoolean","COPY",EDGE,{"derivedFrom":makeQuery(id+"F14.opExtrude","SWEPT_EDGE",EDGE,{"disambiguationData":[OSD([sQuery(id+"F13.wireOp",EDGE,"E60"),sQuery(id+"F13.wireOp",EDGE,"E90")])]})});
            fillet(context, id + "F19", {"entities" : qUnion([Q0, Q1, Q2, Q3, Q4, Q5, Q6, Q7, Q8, Q9, Q10, Q11, Q12, Q13, Q14, Q15, Q16, Q17, Q18, Q19, Q20, Q21, Q22, Q23]), "radius" : 1.5 * mm, "tangentPropagation" : true, "allowEdgeOverflow" : false});
        }
        {
            var Q0;
            Q0=makeQuery(id+"F14.boolean.opBoolean","COPY",EDGE,{"derivedFrom":makeQuery(id+"F14.opExtrude","SWEPT_EDGE",EDGE,{"disambiguationData":[OSD([sQuery(id+"F13.wireOp",EDGE,"E89"),sQuery(id+"F13.wireOp",EDGE,"E96")])]})});
            var Q1;
            Q1=makeQuery(id+"F14.boolean.opBoolean","COPY",EDGE,{"derivedFrom":makeQuery(id+"F14.opExtrude","SWEPT_EDGE",EDGE,{"disambiguationData":[OSD([sQuery(id+"F13.wireOp",EDGE,"E95"),sQuery(id+"F13.wireOp",EDGE,"E96")])]})});
            fillet(context, id + "F20", {"entities" : qUnion([Q0, Q1]), "radius" : 1.5 * mm, "tangentPropagation" : true, "allowEdgeOverflow" : false});
        }
    });
